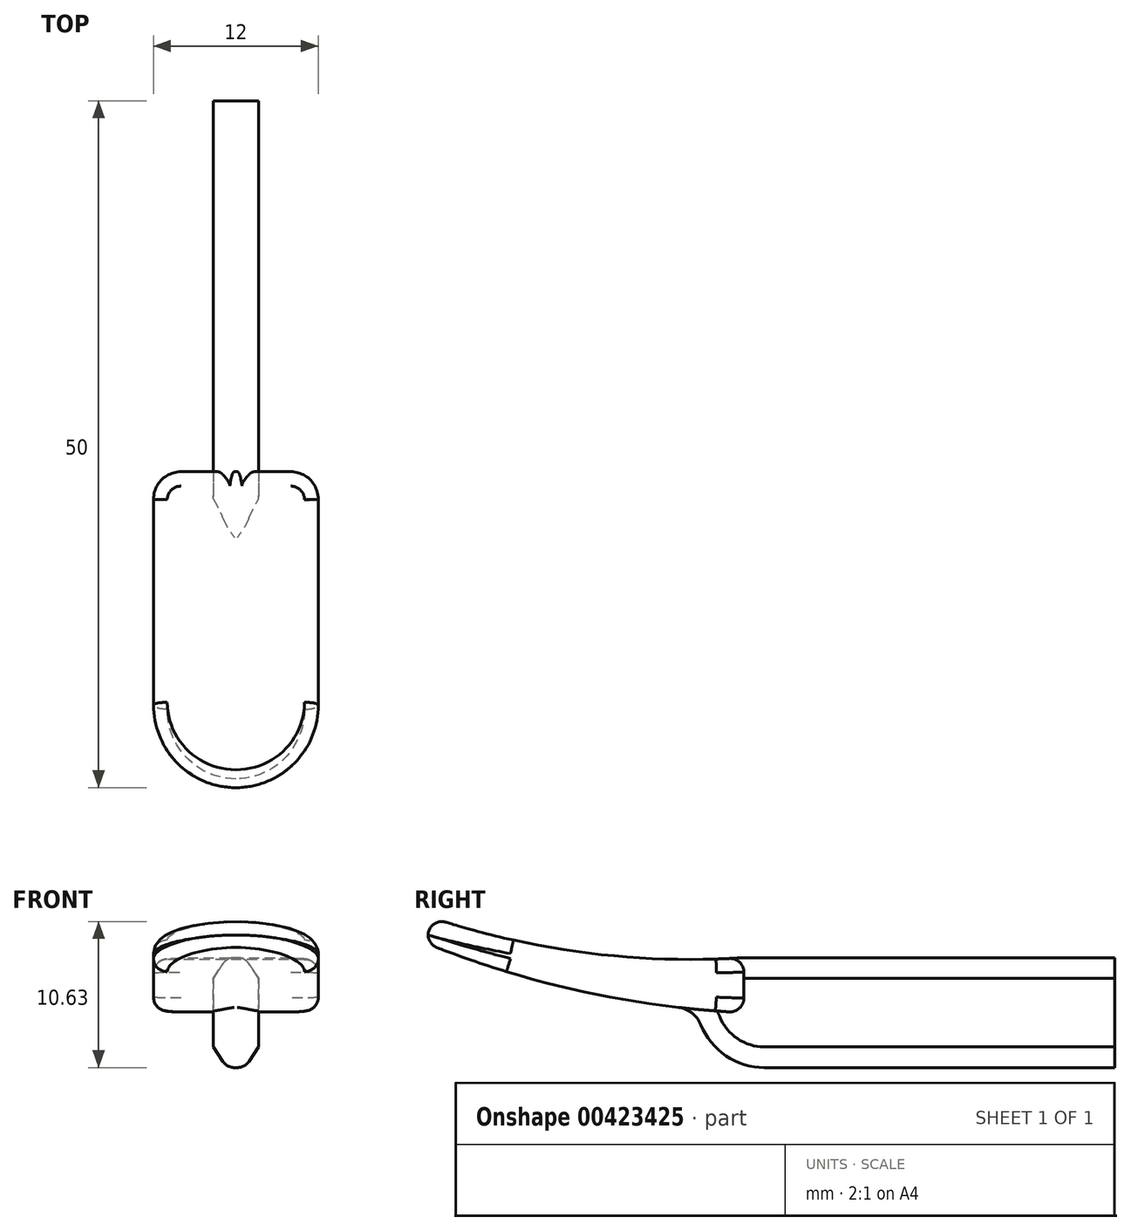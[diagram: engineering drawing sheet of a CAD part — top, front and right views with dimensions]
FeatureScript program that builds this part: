
annotation { "Feature Type Name" : "Feature", "Feature Type Description" : "" }
export const myFeature = defineFeature(function(context is Context, id is Id, definition is map)
    precondition{}
    {
        {
            var Q0;
            Q0=qCreatedBy(makeId("Front.planeOp"),FACE);
            var sketch = newSketch(context, id + "F0", { "sketchPlane" : qUnion([Q0])});
            skLineSegment(sketch, "E0.bottom", {"start": v(1.65, -4) * mm, "end": v(-1.65, -4) * mm});
            skLineSegment(sketch, "E0.top", {"start": v(1.65, 4) * mm, "end": v(-1.65, 4) * mm});
            skLineSegment(sketch, "E0.left", {"start": v(1.65, -4) * mm, "end": v(1.65, 4) * mm});
            skLineSegment(sketch, "E0.right", {"start": v(-1.65, -4) * mm, "end": v(-1.65, 4) * mm});
            skPoint(sketch, "E0.middle", {"position": v(0, 0) * mm});
            skSolve(sketch);
        }
        {
            var Q0;
            Q0 = qSketchRegion(id + "F0", true);
            extrude(context, id + "F1", {"entities" : qUnion([Q0]), "endBound" : BoundingType.SYMMETRIC, "depth" : 30 * mm});
        }
        {
            var Q0;
            Q0=qCreatedBy(makeId("Right.planeOp"),FACE);
            var sketch = newSketch(context, id + "F2", { "sketchPlane" : qUnion([Q0])});
            skArc(sketch, "E1", {"start": v(-35, 7) * mm, "mid": v(-23.65, 4.38) * mm, "end": v(-12, 4) * mm});
            skArc(sketch, "E2", {"start": v(-35, 5) * mm, "mid": v(-23.71, 1.53) * mm, "end": v(-12, 0) * mm});
            skLineSegment(sketch, "E3", {"start": v(-35, 7) * mm, "end": v(-35, 5) * mm});
            skLineSegment(sketch, "E4", {"start": v(-12, 4) * mm, "end": v(-12, 0) * mm});
            skSolve(sketch);
        }
        {
            var Q0;
            Q0=makeQuery(id+"F2.imprint","IMPRINT",FACE,{"disambiguationData":[TD([[makeQuery(id+"F2.imprint","IMPRINT",EDGE,{"derivedFrom":sQuery(id+"F2.wireOp",EDGE,"E1")}),-1.0]])]});
            extrude(context, id + "F3", {"entities" : qUnion([Q0]), "operationType" : NewBodyOperationType.ADD, "endBound" : BoundingType.SYMMETRIC, "depth" : 12 * mm});
        }
        {
            var Q0;
            Q0=makeQuery(id+"F3.opExtrude","CAP_EDGE",EDGE,{"disambiguationData":[OSD([sQuery(id+"F2.wireOp",EDGE,"E3")])],"isStart":false});
            var Q1;
            Q1=makeQuery(id+"F3.opExtrude","CAP_EDGE",EDGE,{"disambiguationData":[OSD([sQuery(id+"F2.wireOp",EDGE,"E3")])],"isStart":true});
            fillet(context, id + "F4", {"entities" : qUnion([Q0, Q1]), "radius" : 6 * mm, "tangentPropagation" : true, "allowEdgeOverflow" : false});
        }
        {
            var Q0;
            Q0=makeQuery(id+"F3.opExtrude","CAP_EDGE",EDGE,{"disambiguationData":[OSD([sQuery(id+"F2.wireOp",EDGE,"E4")])],"isStart":false});
            var Q1;
            Q1=makeQuery(id+"F3.opExtrude","CAP_EDGE",EDGE,{"disambiguationData":[OSD([sQuery(id+"F2.wireOp",EDGE,"E4")])],"isStart":true});
            var Q2;
            Q2=makeQuery(id+"F3.boolean.opBoolean","INTERSECT",EDGE,{"derivedFrom":[makeQuery(id+"F1.opExtrude","CAP_FACE",FACE,{"disambiguationData":[OSD([sQuery(id+"F0.wireOp",EDGE,"E0.bottom"),sQuery(id+"F0.wireOp",EDGE,"E0.top"),sQuery(id+"F0.wireOp",EDGE,"E0.left"),sQuery(id+"F0.wireOp",EDGE,"E0.right")])],"isStart":false}),makeQuery(id+"F3.opExtrude","SWEPT_FACE",FACE,{"disambiguationData":[OSD([sQuery(id+"F2.wireOp",EDGE,"E2")])]})]});
            fillet(context, id + "F5", {"entities" : qUnion([Q0, Q1, Q2]), "radius" : 2 * mm, "tangentPropagation" : true, "allowEdgeOverflow" : false});
        }
        {
            var Q0;
            Q0=makeQuery(id+"F1.opExtrude","CAP_EDGE",EDGE,{"disambiguationData":[OSD([sQuery(id+"F0.wireOp",EDGE,"E0.bottom")])],"isStart":false});
            fillet(context, id + "F6", {"entities" : qUnion([Q0]), "radius" : 5 * mm, "tangentPropagation" : true, "allowEdgeOverflow" : false});
        }
        {
            var Q0;
            Q0=makeQuery(id+"F3.opExtrude","CAP_EDGE",EDGE,{"disambiguationData":[OSD([sQuery(id+"F2.wireOp",EDGE,"E1")])],"isStart":false});
            var Q1;
            Q1=makeQuery(id+"F3.opExtrude","CAP_EDGE",EDGE,{"disambiguationData":[OSD([sQuery(id+"F2.wireOp",EDGE,"E2")])],"isStart":false});
            fillet(context, id + "F7", {"entities" : qUnion([Q0, Q1]), "radius" : 1 * mm, "tangentPropagation" : true, "allowEdgeOverflow" : false});
        }
        {
            var Q0;
            {var subQ0=sQuery(id+"F0.wireOp",EDGE,"E0.top");var subQ1=makeQuery(id+"F1.opExtrude","SWEPT_FACE",FACE,{"disambiguationData":[OSD([subQ0])]});var subQ2=sQuery(id+"F0.wireOp",EDGE,"E0.right");var subQ3=sQuery(id+"F0.wireOp",EDGE,"E0.left");var subQ4=sQuery(id+"F0.wireOp",EDGE,"E0.bottom");var subQ5=makeQuery(id+"F1.opExtrude","CAP_FACE",FACE,{"disambiguationData":[OSD([subQ4,subQ0,subQ3,subQ2])],"isStart":false});var subQ6=makeQuery(id+"F3.opExtrude","SWEPT_FACE",FACE,{"disambiguationData":[OSD([sQuery(id+"F2.wireOp",EDGE,"E1")])]});var subQ7=makeQuery(id+"F1.opExtrude","SWEPT_FACE",FACE,{"disambiguationData":[OSD([subQ2])]});var subQ8=makeQuery(id+"F3.opExtrude","SWEPT_FACE",FACE,{"disambiguationData":[OSD([sQuery(id+"F2.wireOp",EDGE,"E4")])]});Q0=makeQuery(id+"F7.opFillet","MERGE",FACE,{"derivedFrom":[makeQuery(id+"F3.boolean.opBoolean","SPLIT",FACE,{"disambiguationData":[TD([subQ5,subQ1,subQ7,subQ6,subQ8])],"derivedFrom":subQ7}),makeQuery(id+"F3.boolean.opBoolean","SPLIT",FACE,{"disambiguationData":[TD([makeQuery(id+"F1.opExtrude","SWEPT_FACE",FACE,{"disambiguationData":[OSD([subQ4])]}),makeQuery(id+"F1.opExtrude","CAP_FACE",FACE,{"disambiguationData":[OSD([subQ4,subQ0,subQ3,subQ2])],"isStart":true}),subQ5,subQ1,subQ7,subQ6,makeQuery(id+"F3.opExtrude","SWEPT_FACE",FACE,{"disambiguationData":[OSD([sQuery(id+"F2.wireOp",EDGE,"E2")])]}),subQ8])],"derivedFrom":subQ7})]});}
            var sketch = newSketch(context, id + "F8", { "sketchPlane" : qUnion([Q0])});
            skLineSegment(sketch, "E5.0", {"start": v(15, 3.88) * mm, "end": v(15, 4) * mm});
            skPoint(sketch, "E6.0.end.orphan", {"position": v(12, 4) * mm});
            skPoint(sketch, "E7.0.end.orphan", {"position": v(13.05, 3.94) * mm});
            skLineSegment(sketch, "E8", {"start": v(13.05, 3.94) * mm, "end": v(12, 4) * mm});
            skSolve(sketch);
        }
        {
            var Q0;
            Q0 = qSketchRegion(id + "F8", true);
            var Q1;
            Q1=makeQuery(id+"F8.imprint","IMPRINT",FACE,{"disambiguationData":[TD([[makeQuery(id+"F8.imprint","IMPRINT",EDGE,{"derivedFrom":sQuery(id+"F8.wireOp",EDGE,"E5.0")}),1.0]])]});
            extrude(context, id + "F9", {"entities" : qUnion([Q0, Q1]), "operationType" : NewBodyOperationType.REMOVE, "oppositeDirection" : true, "depth" : 3.3 * mm});
        }
        {
            var Q0;
            {var subQ0=sQuery(id+"F0.wireOp",EDGE,"E0.left");var subQ1=sQuery(id+"F0.wireOp",EDGE,"E0.top");Q0=makeQuery(id+"F3.boolean.opBoolean","SPLIT",EDGE,{"disambiguationData":[TD([makeQuery(id+"F1.opExtrude","CAP_FACE",FACE,{"disambiguationData":[OSD([sQuery(id+"F0.wireOp",EDGE,"E0.bottom"),subQ1,subQ0,sQuery(id+"F0.wireOp",EDGE,"E0.right")])],"isStart":true})])],"derivedFrom":makeQuery(id+"F1.opExtrude","SWEPT_EDGE",EDGE,{"disambiguationData":[OSD([subQ1,subQ0])]})});}
            var Q1;
            {var subQ0=sQuery(id+"F0.wireOp",EDGE,"E0.right");var subQ1=sQuery(id+"F0.wireOp",EDGE,"E0.top");Q1=makeQuery(id+"F3.boolean.opBoolean","SPLIT",EDGE,{"disambiguationData":[TD([makeQuery(id+"F1.opExtrude","CAP_FACE",FACE,{"disambiguationData":[OSD([sQuery(id+"F0.wireOp",EDGE,"E0.bottom"),subQ1,sQuery(id+"F0.wireOp",EDGE,"E0.left"),subQ0])],"isStart":true})])],"derivedFrom":makeQuery(id+"F1.opExtrude","SWEPT_EDGE",EDGE,{"disambiguationData":[OSD([subQ1,subQ0])]})});}
            var Q2;
            Q2=makeQuery(id+"F1.opExtrude","SWEPT_EDGE",EDGE,{"disambiguationData":[OSD([sQuery(id+"F0.wireOp",EDGE,"E0.bottom"),sQuery(id+"F0.wireOp",EDGE,"E0.right")])]});
            var Q3;
            Q3=makeQuery(id+"F1.opExtrude","SWEPT_EDGE",EDGE,{"disambiguationData":[OSD([sQuery(id+"F0.wireOp",EDGE,"E0.bottom"),sQuery(id+"F0.wireOp",EDGE,"E0.left")])]});
            chamfer(context, id + "F10", {"entities" : qUnion([Q0, Q1, Q2, Q3]), "chamferType" : ChamferType.TWO_OFFSETS, "width1" : 1 * mm, "oppositeDirection" : false, "width2" : 1.5 * mm, "tangentPropagation" : true});
        }
        {
            var Q0;
            {var subQ0=sQuery(id+"F0.wireOp",EDGE,"E0.top");var subQ1=makeQuery(id+"F1.opExtrude","SWEPT_FACE",FACE,{"disambiguationData":[OSD([subQ0])]});var subQ2=sQuery(id+"F0.wireOp",EDGE,"E0.left");Q0=makeQuery(id+"F10.opChamfer","BLEND_EDGE",EDGE,{"blendedFrom":[makeQuery(id+"F3.boolean.opBoolean","SPLIT",EDGE,{"disambiguationData":[TD([makeQuery(id+"F1.opExtrude","CAP_FACE",FACE,{"disambiguationData":[OSD([sQuery(id+"F0.wireOp",EDGE,"E0.bottom"),subQ0,subQ2,sQuery(id+"F0.wireOp",EDGE,"E0.right")])],"isStart":true})])],"derivedFrom":makeQuery(id+"F1.opExtrude","SWEPT_EDGE",EDGE,{"disambiguationData":[OSD([subQ0,subQ2])]})}),subQ1],"blendedInto":[subQ1]});}
            var Q1;
            {var subQ0=sQuery(id+"F0.wireOp",EDGE,"E0.top");var subQ1=makeQuery(id+"F1.opExtrude","SWEPT_FACE",FACE,{"disambiguationData":[OSD([subQ0])]});var subQ2=sQuery(id+"F0.wireOp",EDGE,"E0.right");Q1=makeQuery(id+"F10.opChamfer","BLEND_EDGE",EDGE,{"blendedFrom":[makeQuery(id+"F3.boolean.opBoolean","SPLIT",EDGE,{"disambiguationData":[TD([makeQuery(id+"F1.opExtrude","CAP_FACE",FACE,{"disambiguationData":[OSD([sQuery(id+"F0.wireOp",EDGE,"E0.bottom"),subQ0,sQuery(id+"F0.wireOp",EDGE,"E0.left"),subQ2])],"isStart":true})])],"derivedFrom":makeQuery(id+"F1.opExtrude","SWEPT_EDGE",EDGE,{"disambiguationData":[OSD([subQ0,subQ2])]})}),subQ1],"blendedInto":[subQ1]});}
            var Q2;
            {var subQ0=sQuery(id+"F0.wireOp",EDGE,"E0.bottom");Q2=makeQuery(id+"F10.opChamfer","BLEND_EDGE",EDGE,{"blendedFrom":[makeQuery(id+"F1.opExtrude","SWEPT_EDGE",EDGE,{"disambiguationData":[OSD([subQ0,sQuery(id+"F0.wireOp",EDGE,"E0.left")])]}),makeQuery(id+"F1.opExtrude","SWEPT_FACE",FACE,{"disambiguationData":[OSD([subQ0])]})],"blendedInto":[makeQuery(id+"F1.opExtrude","SWEPT_FACE",FACE,{"disambiguationData":[OSD([subQ0])]})]});}
            var Q3;
            {var subQ0=sQuery(id+"F0.wireOp",EDGE,"E0.bottom");Q3=makeQuery(id+"F10.opChamfer","BLEND_EDGE",EDGE,{"blendedFrom":[makeQuery(id+"F1.opExtrude","SWEPT_EDGE",EDGE,{"disambiguationData":[OSD([subQ0,sQuery(id+"F0.wireOp",EDGE,"E0.right")])]}),makeQuery(id+"F1.opExtrude","SWEPT_FACE",FACE,{"disambiguationData":[OSD([subQ0])]})],"blendedInto":[makeQuery(id+"F1.opExtrude","SWEPT_FACE",FACE,{"disambiguationData":[OSD([subQ0])]})]});}
            fillet(context, id + "F11", {"entities" : qUnion([Q0, Q1, Q2, Q3]), "radius" : 1 * mm, "tangentPropagation" : true, "allowEdgeOverflow" : false});
        }
    });
